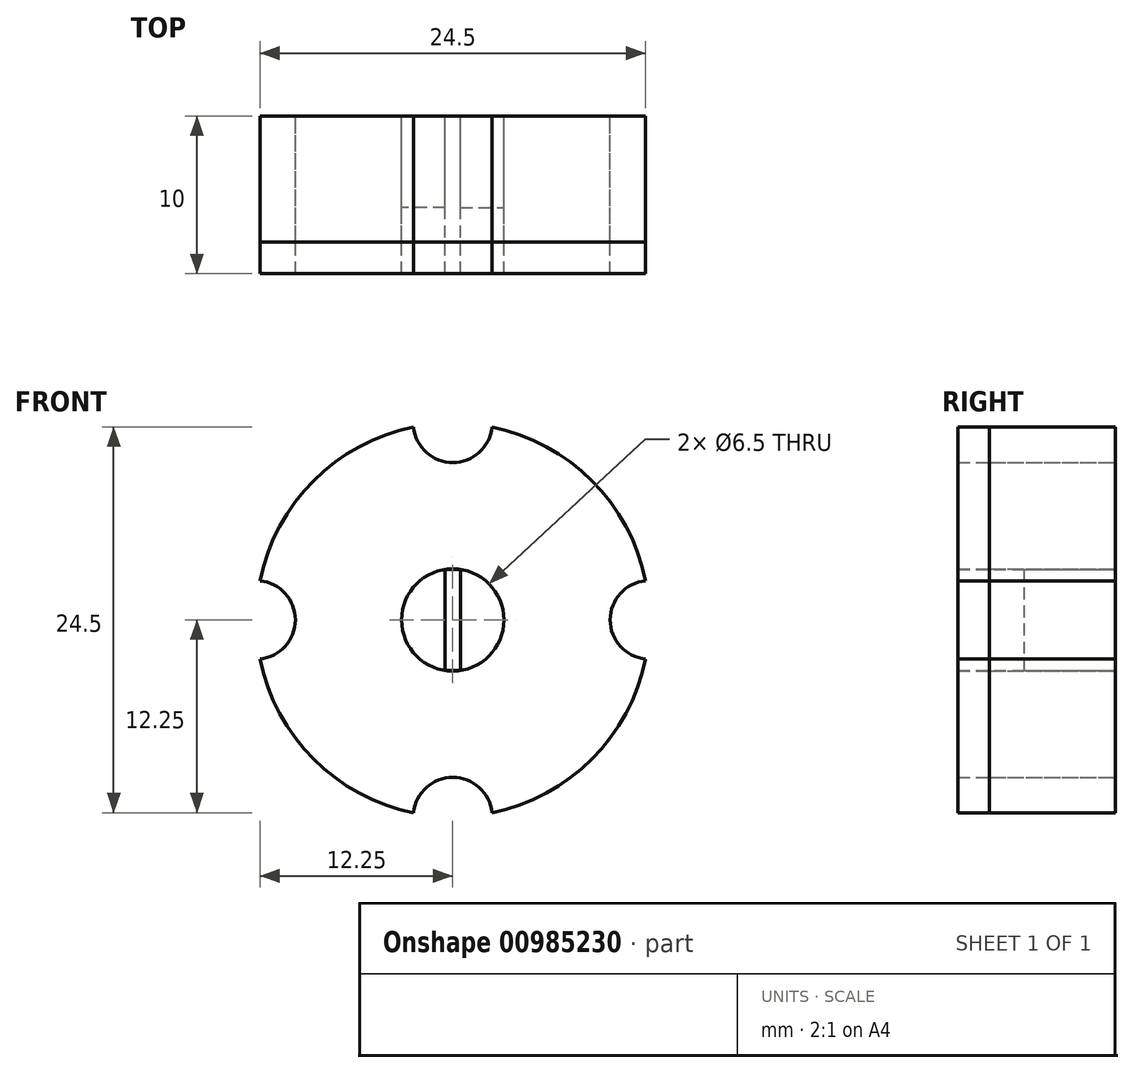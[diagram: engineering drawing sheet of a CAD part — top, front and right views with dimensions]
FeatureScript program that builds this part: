
annotation { "Feature Type Name" : "Feature", "Feature Type Description" : "" }
export const myFeature = defineFeature(function(context is Context, id is Id, definition is map)
    precondition{}
    {
        {
            var Q0;
            Q0=qCreatedBy(makeId("Front.planeOp"),FACE);
            var sketch = newSketch(context, id + "F0", { "sketchPlane" : qUnion([Q0])});
            skCircle(sketch, "E0", {"center": v(0, 0) * mm, "radius": 12.5 * mm});
            skCircle(sketch, "E1", {"center": v(0, 0) * mm, "radius": 3.25 * mm});
            skLineSegment(sketch, "E2.bottom", {"start": v(-0.5, 3.21) * mm, "end": v(0.5, 3.21) * mm});
            skLineSegment(sketch, "E2.top", {"start": v(-0.5, -3.21) * mm, "end": v(0.5, -3.21) * mm});
            skLineSegment(sketch, "E2.left", {"start": v(-0.5, 3.21) * mm, "end": v(-0.5, -3.21) * mm});
            skLineSegment(sketch, "E2.right", {"start": v(0.5, 3.21) * mm, "end": v(0.5, -3.21) * mm});
            skLineSegment(sketch, "E3", {"start": v(0, 0) * mm, "end": v(0, 17.82) * mm, "construction": true});
            skLineSegment(sketch, "E4", {"start": v(0, 0) * mm, "end": v(0, -21.19) * mm, "construction": true});
            skLineSegment(sketch, "E5", {"start": v(0, 0) * mm, "end": v(28.95, 0) * mm, "construction": true});
            skLineSegment(sketch, "E6", {"start": v(0, 0) * mm, "end": v(-26.3, 0) * mm, "construction": true});
            skCircle(sketch, "E7", {"center": v(0, 12.5) * mm, "radius": 2.5 * mm, "construction": true});
            skCircle(sketch, "E8", {"center": v(12.5, 0) * mm, "radius": 2.5 * mm, "construction": true});
            skCircle(sketch, "E9", {"center": v(0, -12.5) * mm, "radius": 2.5 * mm, "construction": true});
            skCircle(sketch, "E10", {"center": v(-12.5, 0) * mm, "radius": 2.5 * mm, "construction": true});
            skSolve(sketch);
        }
        {
            var Q0;
            Q0=makeQuery(id+"F0.imprint","IMPRINT",FACE,{"disambiguationData":[TD([[makeQuery(id+"F0.imprint","IMPRINT",EDGE,{"derivedFrom":sQuery(id+"F0.wireOp",EDGE,"E0")}),1.0]])]});
            var Q1;
            Q1=makeQuery(id+"F0.imprint","IMPRINT",FACE,{"disambiguationData":[TD([[makeQuery(id+"F0.imprint","IMPRINT",EDGE,{"derivedFrom":sQuery(id+"F0.wireOp",EDGE,"E2.bottom")}),-1.0]])]});
            extrude(context, id + "F1", {"entities" : qUnion([Q0, Q1]), "depth" : 10 * mm, "offsetDistance" : 25 * mm});
        }
        {
            var Q0;
            {var subQ0=sQuery(id+"F0.wireOp",EDGE,"E2.right");Q0=makeQuery(id+"F0.imprint","IMPRINT",FACE,{"disambiguationData":[TD([[makeQuery(id+"F0.imprint","IMPRINT",EDGE,{"derivedFrom":subQ0}),1.0]])]});}
            var Q1;
            {var subQ0=sQuery(id+"F0.wireOp",EDGE,"E2.left");Q1=makeQuery(id+"F0.imprint","IMPRINT",FACE,{"disambiguationData":[TD([[makeQuery(id+"F0.imprint","IMPRINT",EDGE,{"derivedFrom":subQ0}),-1.0]])]});}
            extrude(context, id + "F2", {"entities" : qUnion([Q0, Q1]), "depth" : 5.8 * mm, "offsetDistance" : 25 * mm});
        }
        {
            var Q0;
            Q0=sQuery(id+"F0.wireOp",VERTEX,"E7.center");
            var Q1;
            Q1=sQuery(id+"F0.wireOp",VERTEX,"E8.center");
            var Q2;
            Q2=sQuery(id+"F0.wireOp",VERTEX,"E10.center");
            var Q3;
            Q3=sQuery(id+"F0.wireOp",VERTEX,"E9.center");
            var Q4;
            Q4=makeQuery(id+"F1.opExtrude","SWEPT_BODY",BODY,{"disambiguationData":[OSD([sQuery(id+"F0.wireOp",EDGE,"E0"),sQuery(id+"F0.wireOp",EDGE,"E1")])]});
            hole(context, id + "F3", {"style" : HoleStyle.SIMPLE, "endStyle" : HoleEndStyle.THROUGH, "oppositeDirection" : true, "holeDiameter" : 5 * mm, "majorDiameter" : 5 * mm, "isTappedThrough" : true, "tappedDepth" : 12 * mm, "tapClearance" : 3, "locations" : qUnion([Q0, Q1, Q2, Q3]), "scope" : qUnion([Q4])});
        }
        {
            var Q0;
            Q0=makeQuery(id+"F0.imprint","IMPRINT",FACE,{"disambiguationData":[TD([[makeQuery(id+"F0.imprint","IMPRINT",EDGE,{"derivedFrom":sQuery(id+"F0.wireOp",EDGE,"E0")}),1.0]])]});
            extrude(context, id + "F4", {"entities" : qUnion([Q0]), "depth" : 8 * mm, "offsetDistance" : 25 * mm});
        }
        {
            var Q0;
            Q0=sQuery(id+"F0.wireOp",VERTEX,"E7.center");
            var Q1;
            Q1=sQuery(id+"F0.wireOp",VERTEX,"E8.center");
            var Q2;
            Q2=sQuery(id+"F0.wireOp",VERTEX,"E10.center");
            var Q3;
            Q3=sQuery(id+"F0.wireOp",VERTEX,"E9.center");
            var Q4;
            Q4=makeQuery(id+"F4.opExtrude","SWEPT_BODY",BODY,{"disambiguationData":[OSD([sQuery(id+"F0.wireOp",EDGE,"E0"),sQuery(id+"F0.wireOp",EDGE,"E1")])]});
            hole(context, id + "F5", {"style" : HoleStyle.SIMPLE, "endStyle" : HoleEndStyle.THROUGH, "oppositeDirection" : true, "holeDiameter" : 5 * mm, "majorDiameter" : 5 * mm, "isTappedThrough" : true, "tappedDepth" : 12 * mm, "tapClearance" : 3, "locations" : qUnion([Q0, Q1, Q2, Q3]), "scope" : qUnion([Q4])});
        }
    });
